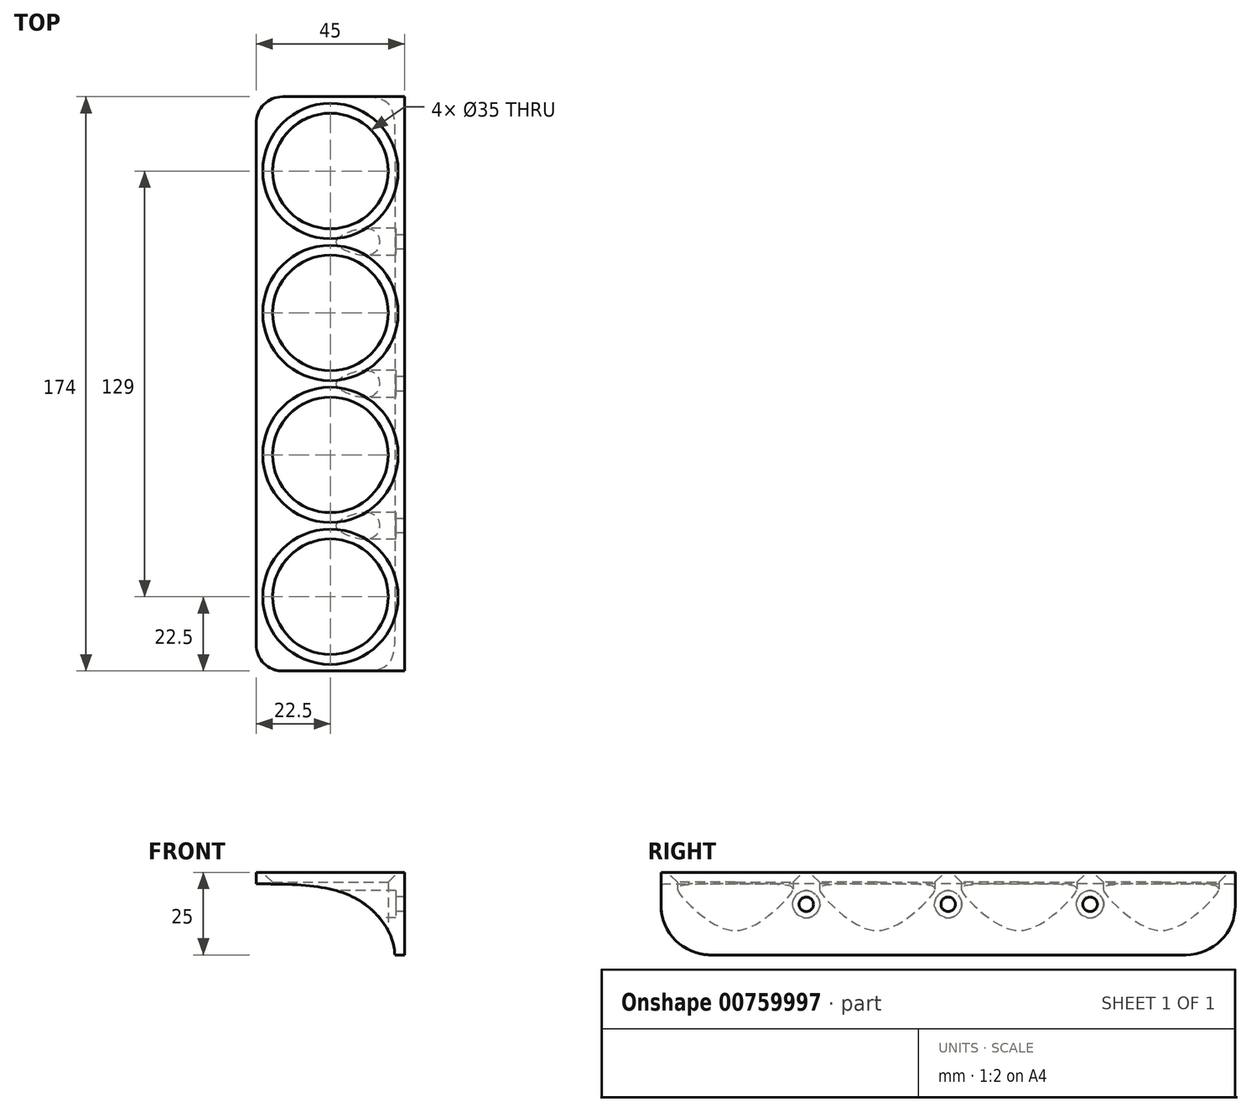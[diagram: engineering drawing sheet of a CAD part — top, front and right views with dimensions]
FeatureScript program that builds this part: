
annotation { "Feature Type Name" : "Feature", "Feature Type Description" : "" }
export const myFeature = defineFeature(function(context is Context, id is Id, definition is map)
    precondition{}
    {
        {
            var Q0;
            Q0=qCreatedBy(makeId("Top.planeOp"),FACE);
            var sketch = newSketch(context, id + "F0", { "sketchPlane" : qUnion([Q0])});
            skLineSegment(sketch, "E0.bottom", {"start": v(22.5, 87) * mm, "end": v(-22.5, 87) * mm});
            skLineSegment(sketch, "E0.top", {"start": v(22.5, -87) * mm, "end": v(-22.5, -87) * mm});
            skLineSegment(sketch, "E0.left", {"start": v(22.5, 87) * mm, "end": v(22.5, -87) * mm});
            skLineSegment(sketch, "E0.right", {"start": v(-22.5, 87) * mm, "end": v(-22.5, -87) * mm});
            skPoint(sketch, "E0.middle", {"position": v(0, 0) * mm});
            skCircle(sketch, "E1", {"center": v(0, 64.5) * mm, "radius": 17.5 * mm});
            skCircle(sketch, "E2.0.1.0", {"center": v(0, 21.5) * mm, "radius": 17.5 * mm});
            skCircle(sketch, "E2.0.2.0", {"center": v(0, -21.5) * mm, "radius": 17.5 * mm});
            skCircle(sketch, "E2.0.3.0", {"center": v(0, -64.5) * mm, "radius": 17.5 * mm});
            skLineSegment(sketch, "E2.direction1", {"start": v(0, 64.5) * mm, "end": v(25.4, 64.5) * mm, "construction": true});
            skLineSegment(sketch, "E2.direction2", {"start": v(0, 64.5) * mm, "end": v(0, 21.5) * mm, "construction": true});
            skLineSegment(sketch, "E3", {"start": v(0, 21.5) * mm, "end": v(0, -21.5) * mm, "construction": true});
            skSolve(sketch);
        }
        {
            var Q0;
            Q0=makeQuery(id+"F0.imprint","IMPRINT",FACE,{"disambiguationData":[TD([[makeQuery(id+"F0.imprint","IMPRINT",EDGE,{"derivedFrom":sQuery(id+"F0.wireOp",EDGE,"E0.bottom")}),1.0]])]});
            extrude(context, id + "F1", {"entities" : qUnion([Q0]), "endBound" : BoundingType.SYMMETRIC, "depth" : 25 * mm, "offsetDistance" : 25 * mm});
        }
        {
            var Q0;
            Q0=qCreatedBy(makeId("Front.planeOp"),FACE);
            var sketch = newSketch(context, id + "F2", { "sketchPlane" : qUnion([Q0])});
            skLineSegment(sketch, "E4.0", {"start": v(-22.5, 12.5) * mm, "end": v(-22.5, -12.5) * mm});
            skLineSegment(sketch, "E5.0", {"start": v(22.5, -12.5) * mm, "end": v(-22.5, -12.5) * mm});
            skFitSpline(sketch, "E6", {"points": [v(19.5, -12.5) * mm, v(9.5, 3.5) * mm, v(-22.5, 9) * mm], "startDerivative": vector(0, 41.61) * mm, "endDerivative": vector(-79.3, 0) * mm});
            skSolve(sketch);
        }
        {
            var Q0;
            {var subQ3=sQuery(id+"F2.wireOp",EDGE,"E6");Q0=makeQuery(id+"F2.imprint","IMPRINT",FACE,{"disambiguationData":[TD([[makeQuery(id+"F2.imprint","IMPRINT",EDGE,{"derivedFrom":subQ3}),1.0]])]});}
            extrude(context, id + "F3", {"entities" : qUnion([Q0]), "operationType" : NewBodyOperationType.REMOVE, "endBound" : BoundingType.THROUGH_ALL, "oppositeDirection" : true, "depth" : 25 * mm, "offsetDistance" : 25 * mm, "hasSecondDirection" : true, "secondDirectionBound" : SecondDirectionBoundingType.THROUGH_ALL, "secondDirectionOppositeDirection" : false, "secondDirectionDepth" : 25 * mm});
        }
        {
            var Q0;
            Q0=makeQuery(id+"F1.opExtrude","SWEPT_FACE",FACE,{"disambiguationData":[OSD([sQuery(id+"F0.wireOp",EDGE,"E0.right")])]});
            var sketch = newSketch(context, id + "F4", { "sketchPlane" : qUnion([Q0])});
            skPoint(sketch, "E7", {"position": v(-43, 2.84) * mm});
            skPoint(sketch, "E8", {"position": v(0, 2.84) * mm});
            skPoint(sketch, "E9", {"position": v(43, 2.84) * mm});
            skFitSpline(sketch, "E10.0", {"points": [v(-65.41, 8.97) * mm, v(-64.5, 8.97) * mm, v(-63.59, 8.97) * mm, v(-62.38, 8.97) * mm, v(-60.9, 8.97) * mm, v(-59.44, 8.96) * mm, v(-58.28, 8.95) * mm, v(-57.16, 8.94) * mm, v(-55.82, 8.93) * mm, v(-54.3, 8.9) * mm, v(-52.86, 8.87) * mm, v(-51.57, 8.82) * mm, v(-50.42, 8.75) * mm, v(-49.4, 8.65) * mm, v(-48.57, 8.52) * mm, v(-47.9, 8.36) * mm, v(-47.41, 8.14) * mm, v(-47.1, 7.86) * mm, v(-46.97, 7.51) * mm, v(-47.03, 7.09) * mm, v(-47.25, 6.57) * mm, v(-47.64, 5.97) * mm, v(-48.18, 5.28) * mm, v(-49.08, 4.24) * mm, v(-50.2, 3.07) * mm, v(-51.54, 1.8) * mm, v(-52.62, 0.83) * mm, v(-53.78, -0.15) * mm, v(-55.03, -1.13) * mm, v(-56.37, -2.1) * mm, v(-57.8, -3) * mm, v(-59.06, -3.7) * mm, v(-60.13, -4.2) * mm, v(-60.96, -4.52) * mm, v(-61.81, -4.79) * mm, v(-62.7, -5) * mm, v(-63.6, -5.13) * mm, v(-64.5, -5.17) * mm, v(-65.42, -5.13) * mm, v(-66.63, -4.95) * mm, v(-67.78, -4.62) * mm, v(-68.9, -4.18) * mm, v(-69.96, -3.69) * mm, v(-71.22, -3) * mm, v(-72.4, -2.23) * mm, v(-73.32, -1.6) * mm, v(-74.19, -0.96) * mm, v(-75.22, -0.14) * mm, v(-76.38, 0.83) * mm, v(-77.46, 1.8) * mm, v(-78.46, 2.75) * mm, v(-79.35, 3.65) * mm, v(-80.14, 4.5) * mm, v(-80.7, 5.13) * mm, v(-81.08, 5.61) * mm, v(-81.59, 6.28) * mm, v(-81.95, 6.93) * mm, v(-82.03, 7.5) * mm, v(-81.9, 7.85) * mm, v(-81.6, 8.13) * mm, v(-81.11, 8.35) * mm, v(-80.44, 8.52) * mm, v(-79.6, 8.65) * mm, v(-78.6, 8.75) * mm, v(-77.05, 8.84) * mm, v(-75.26, 8.9) * mm, v(-73.2, 8.93) * mm, v(-71.58, 8.95) * mm, v(-70.18, 8.96) * mm, v(-69.01, 8.96) * mm, v(-67.82, 8.97) * mm, v(-66.62, 8.97) * mm, v(-65.41, 8.97) * mm, v(-64.5, 8.97) * mm, v(-63.59, 8.97) * mm, v(-65.41, 8.97) * mm]});
            skFitSpline(sketch, "E11.0", {"points": [v(-22.41, 8.97) * mm, v(-21.5, 8.97) * mm, v(-20.59, 8.97) * mm, v(-19.38, 8.97) * mm, v(-17.9, 8.97) * mm, v(-16.44, 8.96) * mm, v(-15.28, 8.95) * mm, v(-14.16, 8.94) * mm, v(-12.82, 8.93) * mm, v(-11.3, 8.9) * mm, v(-9.86, 8.87) * mm, v(-8.57, 8.82) * mm, v(-7.42, 8.75) * mm, v(-6.4, 8.65) * mm, v(-5.57, 8.52) * mm, v(-4.9, 8.36) * mm, v(-4.41, 8.14) * mm, v(-4.1, 7.86) * mm, v(-3.97, 7.51) * mm, v(-4.03, 7.09) * mm, v(-4.25, 6.57) * mm, v(-4.64, 5.97) * mm, v(-5.18, 5.28) * mm, v(-6.08, 4.24) * mm, v(-7.2, 3.07) * mm, v(-8.54, 1.8) * mm, v(-9.62, 0.83) * mm, v(-10.78, -0.15) * mm, v(-12.03, -1.13) * mm, v(-13.37, -2.1) * mm, v(-14.8, -3) * mm, v(-16.06, -3.7) * mm, v(-17.13, -4.2) * mm, v(-17.96, -4.52) * mm, v(-18.81, -4.79) * mm, v(-19.7, -5) * mm, v(-20.6, -5.13) * mm, v(-21.5, -5.17) * mm, v(-22.42, -5.13) * mm, v(-23.63, -4.95) * mm, v(-24.78, -4.62) * mm, v(-25.9, -4.18) * mm, v(-26.96, -3.69) * mm, v(-28.22, -3) * mm, v(-29.4, -2.23) * mm, v(-30.32, -1.6) * mm, v(-31.19, -0.96) * mm, v(-32.22, -0.14) * mm, v(-33.38, 0.83) * mm, v(-34.46, 1.8) * mm, v(-35.46, 2.75) * mm, v(-36.35, 3.65) * mm, v(-37.14, 4.5) * mm, v(-37.7, 5.13) * mm, v(-38.08, 5.61) * mm, v(-38.59, 6.28) * mm, v(-38.95, 6.93) * mm, v(-39.03, 7.5) * mm, v(-38.9, 7.85) * mm, v(-38.6, 8.13) * mm, v(-38.11, 8.35) * mm, v(-37.44, 8.52) * mm, v(-36.6, 8.65) * mm, v(-35.6, 8.75) * mm, v(-34.05, 8.84) * mm, v(-32.26, 8.9) * mm, v(-30.2, 8.93) * mm, v(-28.58, 8.95) * mm, v(-27.18, 8.96) * mm, v(-26.01, 8.96) * mm, v(-24.82, 8.97) * mm, v(-23.62, 8.97) * mm, v(-22.41, 8.97) * mm, v(-21.5, 8.97) * mm, v(-20.59, 8.97) * mm, v(-22.41, 8.97) * mm]});
            skLineSegment(sketch, "E12", {"start": v(-21.5, -5.16) * mm, "end": v(-64.5, -5.16) * mm});
            skLineSegment(sketch, "E13", {"start": v(-43, -5.16) * mm, "end": v(-43, 2.84) * mm});
            skSolve(sketch);
        }
        {
            var Q0;
            Q0=sQuery(id+"F4.wireOp",VERTEX,"E7");
            var Q1;
            Q1=sQuery(id+"F4.wireOp",VERTEX,"E8");
            var Q2;
            Q2=sQuery(id+"F4.wireOp",VERTEX,"E9");
            var Q3;
            Q3=makeQuery(id+"F1.opExtrude","SWEPT_BODY",BODY,{"disambiguationData":[OSD([sQuery(id+"F0.wireOp",EDGE,"E0.bottom"),sQuery(id+"F0.wireOp",EDGE,"E0.top"),sQuery(id+"F0.wireOp",EDGE,"E0.left"),sQuery(id+"F0.wireOp",EDGE,"E0.right"),sQuery(id+"F0.wireOp",EDGE,"E1"),sQuery(id+"F0.wireOp",EDGE,"E2.0.1.0"),sQuery(id+"F0.wireOp",EDGE,"E2.0.2.0"),sQuery(id+"F0.wireOp",EDGE,"E2.0.3.0")])]});
            hole(context, id + "F5", {"style" : HoleStyle.C_BORE, "endStyle" : HoleEndStyle.THROUGH, "holeDiameter" : 4.4 * mm, "cBoreDiameter" : 8.25 * mm, "cBoreDepth" : 5 * mm, "majorDiameter" : 5 * mm, "isTappedThrough" : true, "tappedDepth" : 12 * mm, "tapClearance" : 3, "locations" : qUnion([Q0, Q1, Q2]), "scope" : qUnion([Q3])});
        }
        {
            var Q0;
            Q0=makeQuery(id+"F1.opExtrude","CAP_EDGE",EDGE,{"disambiguationData":[OSD([sQuery(id+"F0.wireOp",EDGE,"E1")])],"isStart":false});
            var Q1;
            Q1=makeQuery(id+"F1.opExtrude","CAP_EDGE",EDGE,{"disambiguationData":[OSD([sQuery(id+"F0.wireOp",EDGE,"E2.0.1.0")])],"isStart":false});
            var Q2;
            Q2=makeQuery(id+"F1.opExtrude","CAP_EDGE",EDGE,{"disambiguationData":[OSD([sQuery(id+"F0.wireOp",EDGE,"E2.0.2.0")])],"isStart":false});
            var Q3;
            Q3=makeQuery(id+"F1.opExtrude","CAP_EDGE",EDGE,{"disambiguationData":[OSD([sQuery(id+"F0.wireOp",EDGE,"E2.0.3.0")])],"isStart":false});
            chamfer(context, id + "F6", {"entities" : qUnion([Q0, Q1, Q2, Q3]), "width" : 3 * mm, "tangentPropagation" : true});
        }
        {
            var Q0;
            Q0=makeQuery(id+"F1.opExtrude","CAP_EDGE",EDGE,{"disambiguationData":[OSD([sQuery(id+"F0.wireOp",EDGE,"E0.top")])],"isStart":true});
            var Q1;
            Q1=makeQuery(id+"F1.opExtrude","CAP_EDGE",EDGE,{"disambiguationData":[OSD([sQuery(id+"F0.wireOp",EDGE,"E0.bottom")])],"isStart":true});
            fillet(context, id + "F7", {"entities" : qUnion([Q0, Q1]), "radius" : 15 * mm, "tangentPropagation" : true, "allowEdgeOverflow" : false});
        }
        {
            var Q0;
            Q0=makeQuery(id+"F1.opExtrude","SWEPT_EDGE",EDGE,{"disambiguationData":[OSD([sQuery(id+"F0.wireOp",EDGE,"E0.bottom"),sQuery(id+"F0.wireOp",EDGE,"E0.right")])]});
            var Q1;
            Q1=makeQuery(id+"F1.opExtrude","SWEPT_EDGE",EDGE,{"disambiguationData":[OSD([sQuery(id+"F0.wireOp",EDGE,"E0.top"),sQuery(id+"F0.wireOp",EDGE,"E0.right")])]});
            fillet(context, id + "F8", {"entities" : qUnion([Q0, Q1]), "radius" : 8 * mm, "tangentPropagation" : true, "allowEdgeOverflow" : false});
        }
    });
